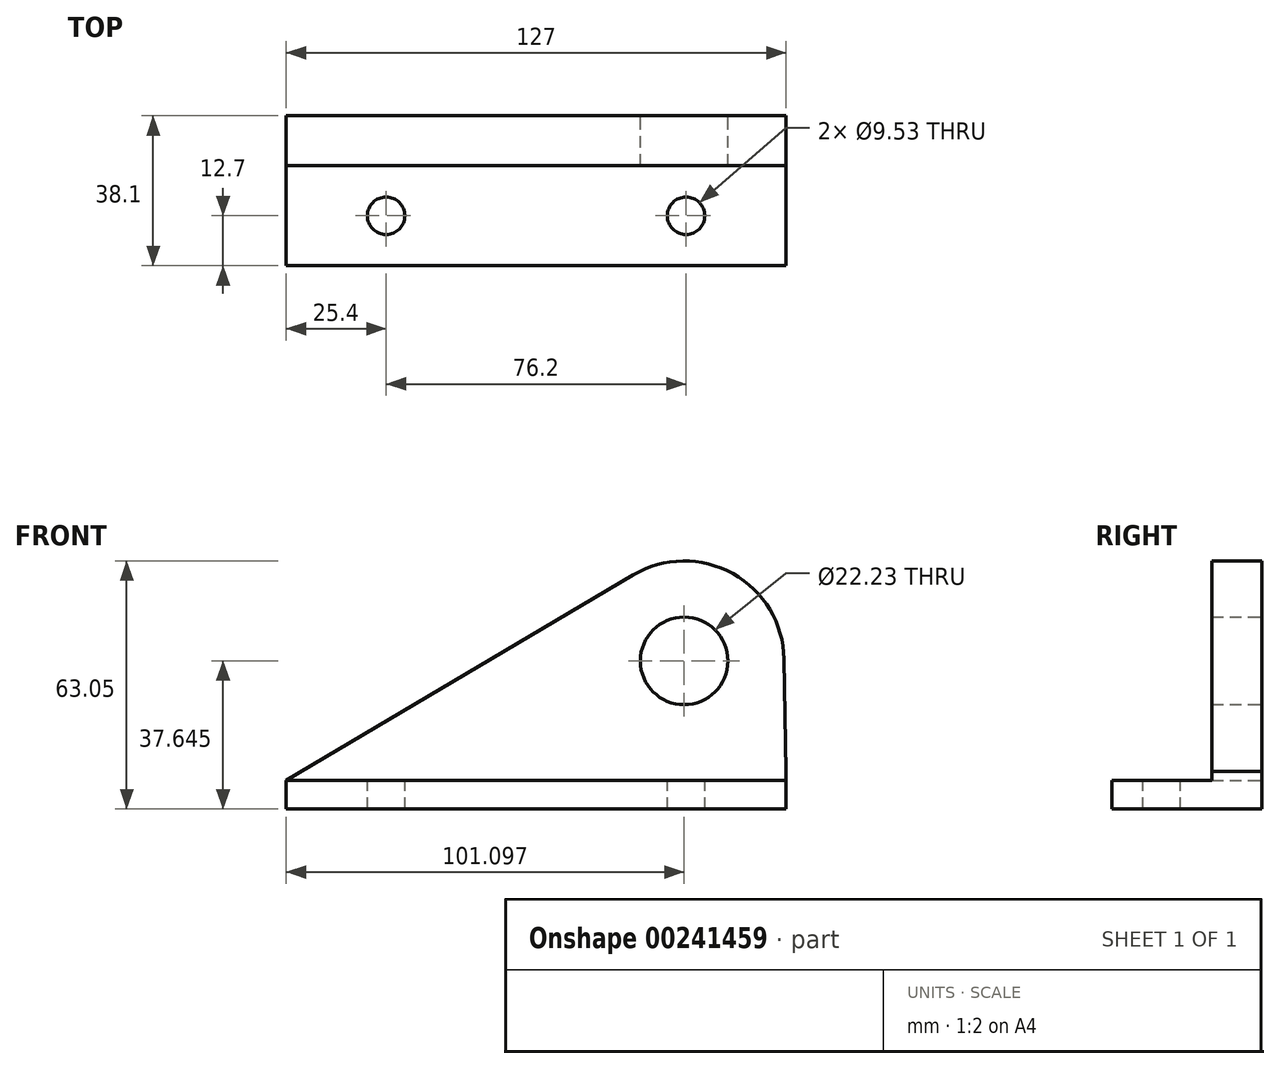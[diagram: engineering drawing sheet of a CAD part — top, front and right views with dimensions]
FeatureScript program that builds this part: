
annotation { "Feature Type Name" : "Feature", "Feature Type Description" : "" }
export const myFeature = defineFeature(function(context is Context, id is Id, definition is map)
    precondition{}
    {
        {
            var Q0;
            Q0=qCreatedBy(makeId("Front.planeOp"),FACE);
            var sketch = newSketch(context, id + "F0", { "sketchPlane" : qUnion([Q0])});
            skLineSegment(sketch, "E0", {"start": v(0, 0) * mm, "end": v(127, 0) * mm});
            skLineSegment(sketch, "E1", {"start": v(127, 0) * mm, "end": v(127, 9.52) * mm});
            skLineSegment(sketch, "E2", {"start": v(0, 7.27) * mm, "end": v(0, 0) * mm});
            skArc(sketch, "E3", {"start": v(126.5, 38.1) * mm, "mid": v(113.48, 59.82) * mm, "end": v(88.15, 59.5) * mm});
            skLineSegment(sketch, "E4", {"start": v(127, 9.53) * mm, "end": v(126.5, 38.1) * mm});
            skLineSegment(sketch, "E5", {"start": v(0, 7.27) * mm, "end": v(88.15, 59.5) * mm});
            skLineSegment(sketch, "E6", {"start": v(0, 7.27) * mm, "end": v(127, 7.27) * mm});
            skLineSegment(sketch, "E7", {"start": v(127, 7.27) * mm, "end": v(101.6, 7.27) * mm});
            skSolve(sketch);
        }
        {
            var Q0;
            {var subQ1=sQuery(id+"F0.wireOp",EDGE,"E0");Q0=makeQuery(id+"F0.imprint","IMPRINT",FACE,{"disambiguationData":[TD([[makeQuery(id+"F0.imprint","IMPRINT",EDGE,{"derivedFrom":subQ1}),1.0]])]});}
            extrude(context, id + "F1", {"entities" : qUnion([Q0]), "depth" : 38.1 * mm});
        }
        {
            var Q0;
            Q0=makeQuery(id+"F0.imprint","IMPRINT",FACE,{"disambiguationData":[TD([[makeQuery(id+"F0.imprint","IMPRINT",EDGE,{"derivedFrom":sQuery(id+"F0.wireOp",EDGE,"E3")}),1.0]])]});
            extrude(context, id + "F2", {"entities" : qUnion([Q0]), "operationType" : NewBodyOperationType.ADD, "depth" : 12.7 * mm});
        }
        {
            var Q0;
            Q0=sQuery(id+"F0.wireOp",VERTEX,"E3.center");
            var Q1;
            Q1=makeQuery(id+"F1.opExtrude","SWEPT_BODY",BODY,{"disambiguationData":[OSD([sQuery(id+"F0.wireOp",EDGE,"E0"),sQuery(id+"F0.wireOp",EDGE,"E1"),sQuery(id+"F0.wireOp",EDGE,"E2"),sQuery(id+"F0.wireOp",EDGE,"E6"),sQuery(id+"F0.wireOp",EDGE,"E7")])]});
            hole(context, id + "F3", {"style" : HoleStyle.SIMPLE, "endStyle" : HoleEndStyle.THROUGH, "oppositeDirection" : true, "holeDiameter" : 22.22 * mm, "locations" : qUnion([Q0]), "scope" : qUnion([Q1]), "isTappedThrough" : true});
        }
        {
            var Q0;
            Q0=makeQuery(id+"F1.opExtrude","SWEPT_FACE",FACE,{"disambiguationData":[OSD([sQuery(id+"F0.wireOp",EDGE,"E6"),sQuery(id+"F0.wireOp",EDGE,"E7")])]});
            var sketch = newSketch(context, id + "F4", { "sketchPlane" : qUnion([Q0])});
            skLineSegment(sketch, "E8", {"start": v(0, -38.1) * mm, "end": v(0, -25.4) * mm});
            skPoint(sketch, "E9.end.orphan", {"position": v(127, -25.4) * mm});
            skLineSegment(sketch, "E10", {"start": v(0, -25.4) * mm, "end": v(25.4, -25.4) * mm});
            skLineSegment(sketch, "E11", {"start": v(25.4, -25.4) * mm, "end": v(101.6, -25.4) * mm});
            skPoint(sketch, "E11.endSnap0", {"position": v(12.7, -25.4) * mm});
            skSolve(sketch);
        }
        {
            var Q0;
            Q0=sQuery(id+"F4.wireOp",VERTEX,"E10.end");
            var Q1;
            Q1=sQuery(id+"F4.wireOp",VERTEX,"E11.end");
            var Q2;
            Q2=makeQuery(id+"F1.opExtrude","SWEPT_BODY",BODY,{"disambiguationData":[OSD([sQuery(id+"F0.wireOp",EDGE,"E0"),sQuery(id+"F0.wireOp",EDGE,"E1"),sQuery(id+"F0.wireOp",EDGE,"E2"),sQuery(id+"F0.wireOp",EDGE,"E6"),sQuery(id+"F0.wireOp",EDGE,"E7")])]});
            hole(context, id + "F5", {"style" : HoleStyle.SIMPLE, "endStyle" : HoleEndStyle.THROUGH, "holeDiameter" : 9.52 * mm, "locations" : qUnion([Q0, Q1]), "scope" : qUnion([Q2]), "isTappedThrough" : true});
        }
    });
